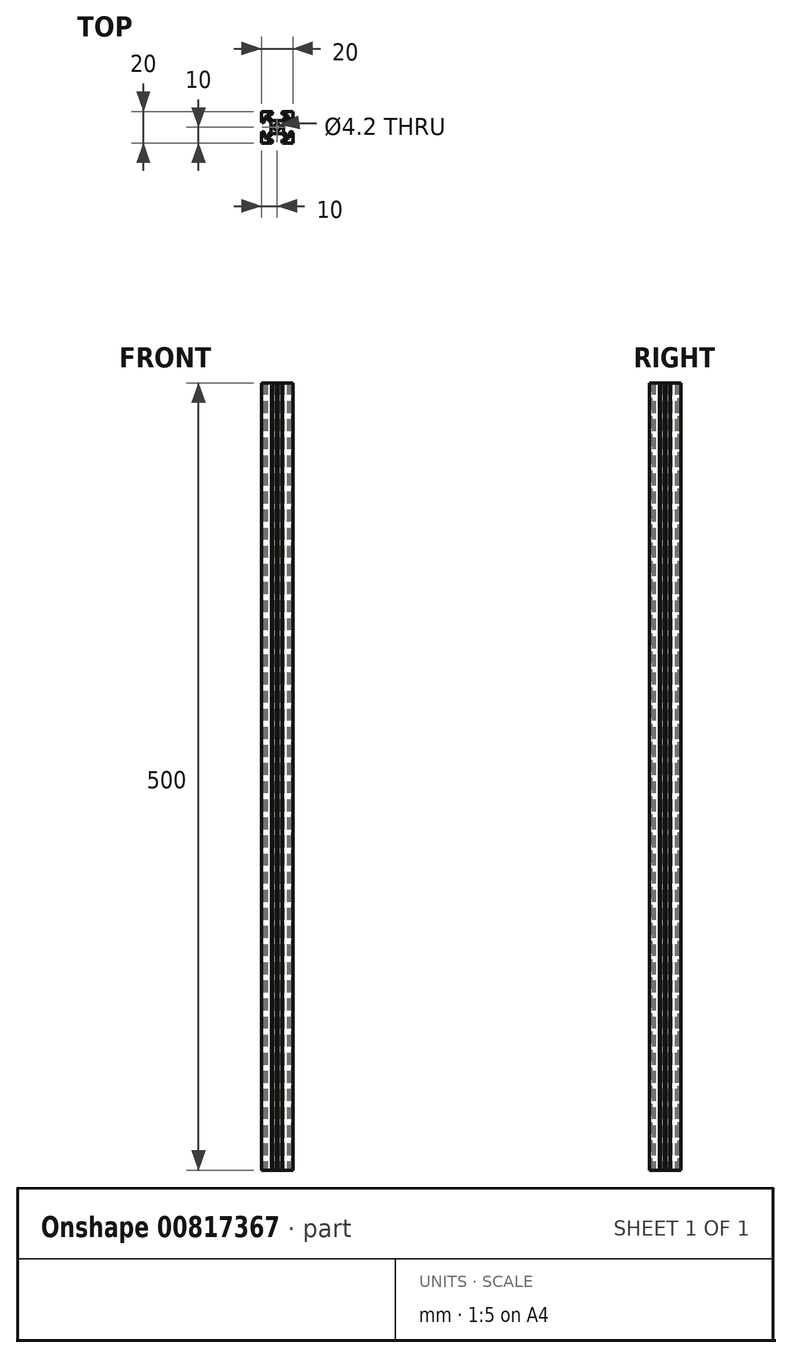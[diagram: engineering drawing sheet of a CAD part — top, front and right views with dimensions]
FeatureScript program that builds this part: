
annotation { "Feature Type Name" : "Feature", "Feature Type Description" : "" }
export const myFeature = defineFeature(function(context is Context, id is Id, definition is map)
    precondition{}
    {
        {
            assignVariable(context, id + "F0", {"name" : "length", "anyValue" : 500});
        }
        {
            var Q0;
            Q0=qCreatedBy(makeId("Top.planeOp"),FACE);
            var sketch = newSketch(context, id + "F1", { "sketchPlane" : qUnion([Q0])});
            skLineSegment(sketch, "E0", {"start": v(0, 0) * mm, "end": v(0, 4) * mm});
            skLineSegment(sketch, "E1", {"start": v(0, 4) * mm, "end": v(3, 4) * mm});
            skLineSegment(sketch, "E2", {"start": v(3, 4) * mm, "end": v(6.5, 7.5) * mm});
            skLineSegment(sketch, "E3", {"start": v(6.5, 7.5) * mm, "end": v(6.5, 8) * mm});
            skLineSegment(sketch, "E4", {"start": v(6.5, 8) * mm, "end": v(3, 8) * mm});
            skLineSegment(sketch, "E5", {"start": v(3, 8) * mm, "end": v(3, 10) * mm});
            skLineSegment(sketch, "E6", {"start": v(3, 10) * mm, "end": v(10, 10) * mm});
            skLineSegment(sketch, "E7", {"start": v(10, 10) * mm, "end": v(10, 3) * mm});
            skLineSegment(sketch, "E8", {"start": v(10, 3) * mm, "end": v(8, 3) * mm});
            skLineSegment(sketch, "E9", {"start": v(8, 3) * mm, "end": v(8, 6.5) * mm});
            skLineSegment(sketch, "E10", {"start": v(8, 6.5) * mm, "end": v(7.5, 6.5) * mm});
            skLineSegment(sketch, "E11", {"start": v(7.5, 6.5) * mm, "end": v(4, 3) * mm});
            skLineSegment(sketch, "E12", {"start": v(4, 3) * mm, "end": v(4, 0) * mm});
            skLineSegment(sketch, "E13", {"start": v(4, 0) * mm, "end": v(0, 0) * mm});
            skLineSegment(sketch, "E14", {"start": v(-1.28, 4) * mm, "end": v(-1.28, 8) * mm, "construction": true});
            skLineSegment(sketch, "E15", {"start": v(0, -0.9) * mm, "end": v(10, -0.9) * mm, "construction": true});
            skArc(sketch, "E16", {"start": v(2.1, 0) * mm, "mid": v(1.48, 1.48) * mm, "end": v(0, 2.1) * mm});
            skSolve(sketch);
        }
        {
            var Q0;
            {var subQ0=sQuery(id+"F1.wireOp",EDGE,"E1");Q0=makeQuery(id+"F1.imprint","IMPRINT",FACE,{"disambiguationData":[TD([[makeQuery(id+"F1.imprint","IMPRINT",EDGE,{"derivedFrom":subQ0}),-1.0]])]});}
            extrude(context, id + "F2", {"entities" : qUnion([Q0]), "depth" : (getVariable(context, 'length')) * mm, "offsetDistance" : 25 * mm});
        }
        {
            var Q0;
            Q0=makeQuery(id+"F2.opExtrude","SWEPT_EDGE",EDGE,{"disambiguationData":[OSD([sQuery(id+"F1.wireOp",EDGE,"E0"),sQuery(id+"F1.wireOp",EDGE,"E1")])]});
            var Q1;
            Q1=makeQuery(id+"F2.opExtrude","SWEPT_EDGE",EDGE,{"disambiguationData":[OSD([sQuery(id+"F1.wireOp",EDGE,"E12"),sQuery(id+"F1.wireOp",EDGE,"E13")])]});
            var Q2;
            Q2=makeQuery(id+"F2.opExtrude","SWEPT_EDGE",EDGE,{"disambiguationData":[OSD([sQuery(id+"F1.wireOp",EDGE,"E4"),sQuery(id+"F1.wireOp",EDGE,"E5")])]});
            var Q3;
            Q3=makeQuery(id+"F2.opExtrude","SWEPT_EDGE",EDGE,{"disambiguationData":[OSD([sQuery(id+"F1.wireOp",EDGE,"E8"),sQuery(id+"F1.wireOp",EDGE,"E9")])]});
            var Q4;
            Q4=makeQuery(id+"F2.opExtrude","SWEPT_EDGE",EDGE,{"disambiguationData":[OSD([sQuery(id+"F1.wireOp",EDGE,"E7"),sQuery(id+"F1.wireOp",EDGE,"E8")])]});
            var Q5;
            Q5=makeQuery(id+"F2.opExtrude","SWEPT_EDGE",EDGE,{"disambiguationData":[OSD([sQuery(id+"F1.wireOp",EDGE,"E5"),sQuery(id+"F1.wireOp",EDGE,"E6")])]});
            chamfer(context, id + "F3", {"entities" : qUnion([Q0, Q1, Q2, Q3, Q4, Q5]), "width" : .5 * mm, "tangentPropagation" : true});
        }
        {
            var Q0;
            Q0=makeQuery(id+"F2.opExtrude","SWEPT_BODY",BODY,{"disambiguationData":[OSD([sQuery(id+"F1.wireOp",EDGE,"E0"),sQuery(id+"F1.wireOp",EDGE,"E1"),sQuery(id+"F1.wireOp",EDGE,"E2"),sQuery(id+"F1.wireOp",EDGE,"E3"),sQuery(id+"F1.wireOp",EDGE,"E4"),sQuery(id+"F1.wireOp",EDGE,"E5"),sQuery(id+"F1.wireOp",EDGE,"E6"),sQuery(id+"F1.wireOp",EDGE,"E7"),sQuery(id+"F1.wireOp",EDGE,"E8"),sQuery(id+"F1.wireOp",EDGE,"E9"),sQuery(id+"F1.wireOp",EDGE,"E10"),sQuery(id+"F1.wireOp",EDGE,"E11"),sQuery(id+"F1.wireOp",EDGE,"E12"),sQuery(id+"F1.wireOp",EDGE,"E13"),sQuery(id+"F1.wireOp",EDGE,"E16")])]});
            var Q1;
            Q1=makeQuery(id+"F2.opExtrude","SWEPT_FACE",FACE,{"disambiguationData":[OSD([sQuery(id+"F1.wireOp",EDGE,"E0")])]});
            mirror(context, id + "F4", {"operationType" : NewBodyOperationType.ADD, "entities" : qUnion([Q0]), "mirrorPlane" : qUnion([Q1])});
        }
        {
            var Q0;
            Q0=makeQuery(id+"F2.opExtrude","SWEPT_BODY",BODY,{"disambiguationData":[OSD([sQuery(id+"F1.wireOp",EDGE,"E0"),sQuery(id+"F1.wireOp",EDGE,"E1"),sQuery(id+"F1.wireOp",EDGE,"E2"),sQuery(id+"F1.wireOp",EDGE,"E3"),sQuery(id+"F1.wireOp",EDGE,"E4"),sQuery(id+"F1.wireOp",EDGE,"E5"),sQuery(id+"F1.wireOp",EDGE,"E6"),sQuery(id+"F1.wireOp",EDGE,"E7"),sQuery(id+"F1.wireOp",EDGE,"E8"),sQuery(id+"F1.wireOp",EDGE,"E9"),sQuery(id+"F1.wireOp",EDGE,"E10"),sQuery(id+"F1.wireOp",EDGE,"E11"),sQuery(id+"F1.wireOp",EDGE,"E12"),sQuery(id+"F1.wireOp",EDGE,"E13"),sQuery(id+"F1.wireOp",EDGE,"E16")])]});
            var Q1;
            Q1=makeQuery(id+"F4.opPattern","COPY",FACE,{"derivedFrom":makeQuery(id+"F2.opExtrude","SWEPT_FACE",FACE,{"disambiguationData":[OSD([sQuery(id+"F1.wireOp",EDGE,"E13")])]}),"instanceName":"1"});
            mirror(context, id + "F5", {"operationType" : NewBodyOperationType.ADD, "entities" : qUnion([Q0]), "mirrorPlane" : qUnion([Q1])});
        }
    });
